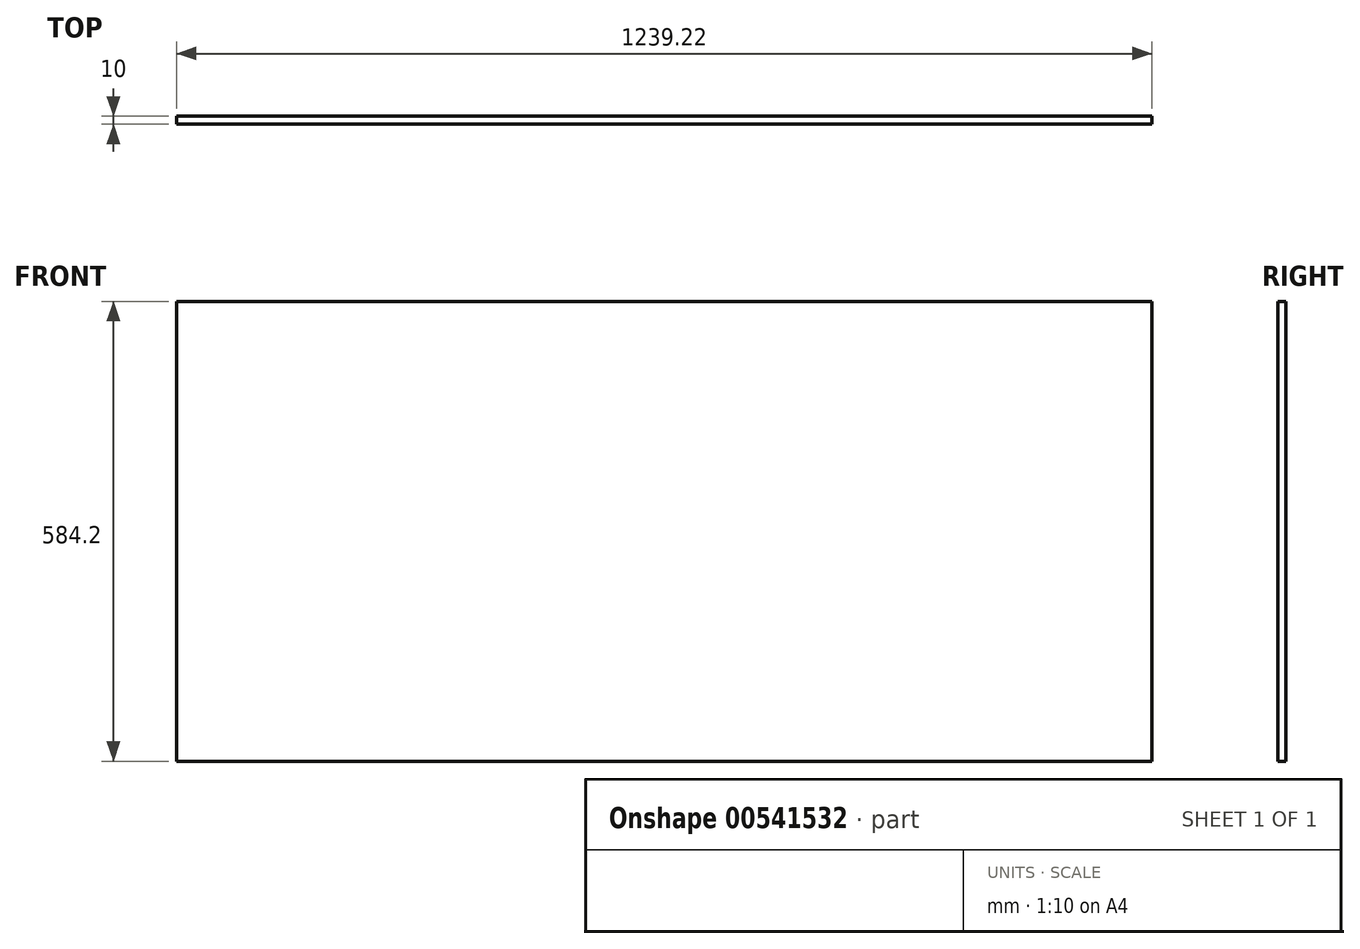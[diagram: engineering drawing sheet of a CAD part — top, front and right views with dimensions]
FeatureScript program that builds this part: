
annotation { "Feature Type Name" : "Feature", "Feature Type Description" : "" }
export const myFeature = defineFeature(function(context is Context, id is Id, definition is map)
    precondition{}
    {
        {
            var Q0;
            Q0=qCreatedBy(makeId("Front.planeOp"),FACE);
            var sketch = newSketch(context, id + "F0", { "sketchPlane" : qUnion([Q0])});
            skLineSegment(sketch, "E0.bottom", {"start": v(619.6, -292.1) * mm, "end": v(-619.6, -292.1) * mm});
            skLineSegment(sketch, "E0.top", {"start": v(619.6, 292.1) * mm, "end": v(-619.6, 292.1) * mm});
            skLineSegment(sketch, "E0.left", {"start": v(619.6, -292.1) * mm, "end": v(619.6, 292.1) * mm});
            skLineSegment(sketch, "E0.right", {"start": v(-619.6, -292.1) * mm, "end": v(-619.6, 292.1) * mm});
            skPoint(sketch, "E0.middle", {"position": v(0, 0) * mm});
            skSolve(sketch);
        }
        {
            var Q0;
            Q0=makeQuery(id+"F0.imprint","IMPRINT",FACE,{"disambiguationData":[TD([[makeQuery(id+"F0.imprint","IMPRINT",EDGE,{"derivedFrom":sQuery(id+"F0.wireOp",EDGE,"E0.bottom")}),-1.0]])]});
            extrude(context, id + "F1", {"entities" : qUnion([Q0]), "depth" : 10 * mm});
        }
    });
